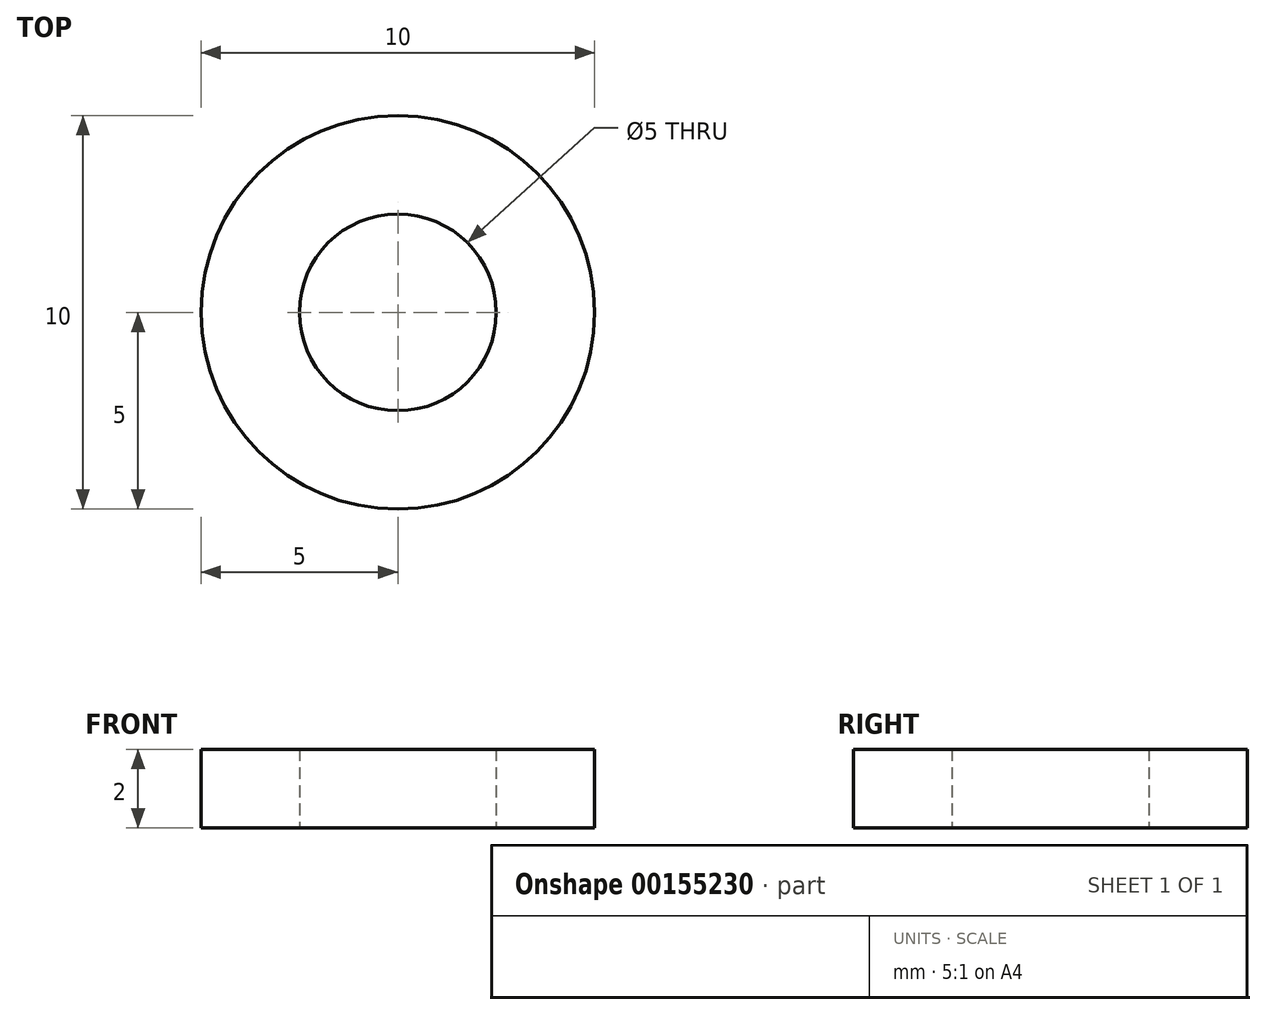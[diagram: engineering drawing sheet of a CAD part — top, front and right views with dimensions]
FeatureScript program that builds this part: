
annotation { "Feature Type Name" : "Feature", "Feature Type Description" : "" }
export const myFeature = defineFeature(function(context is Context, id is Id, definition is map)
    precondition{}
    {
        {
            var Q0;
            Q0=qCreatedBy(makeId("Top.planeOp"),FACE);
            var sketch = newSketch(context, id + "F0", { "sketchPlane" : qUnion([Q0])});
            skCircle(sketch, "E0", {"center": v(0, 0) * mm, "radius": 5 * mm});
            skCircle(sketch, "E1", {"center": v(0, 0) * mm, "radius": 2.5 * mm});
            skSolve(sketch);
        }
        {
            var Q0;
            Q0 = qSketchRegion(id + "F0", true);
            extrude(context, id + "F1", {"entities" : qUnion([Q0]), "depth" : 2 * mm});
        }
    });
